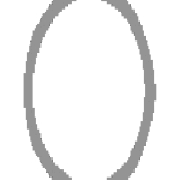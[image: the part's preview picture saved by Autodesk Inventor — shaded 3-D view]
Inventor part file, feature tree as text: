
AUTODESK INVENTOR PART (.ipt)
format: ipt  version: 2021 (Build 250183000, 183)  size: 112,128 bytes
history: native  units: in
note: dims shown in document units (in); Inventor stores cm internally (conversion verified against a paired STEP export)
features: other x4, sketch x3, plane x1
ambient origin geometry x8: Origin, YZ Plane, XZ Plane, XY Plane, X Axis, Y Axis, Z Axis, Center Point
bodies: Solid1 (feature_tree), Body (feature_tree)
feature tree (8):
  other  "Driven Length"
  other  "Frame Generator"
  other  "Start Plane"
  other  "End Plane"
  sketch  "Sketch"  dims[d2=6.0in d4=-0.0in d5=6.0in d6=0.12in d7=0.0in d8=90.0deg d9=6.0in]
  sketch  "Sketch2"  dims[d0=1.0in]
  plane  "Work Plane3"
  sketch  "Sketch3"  dims[d1=0.065in]
